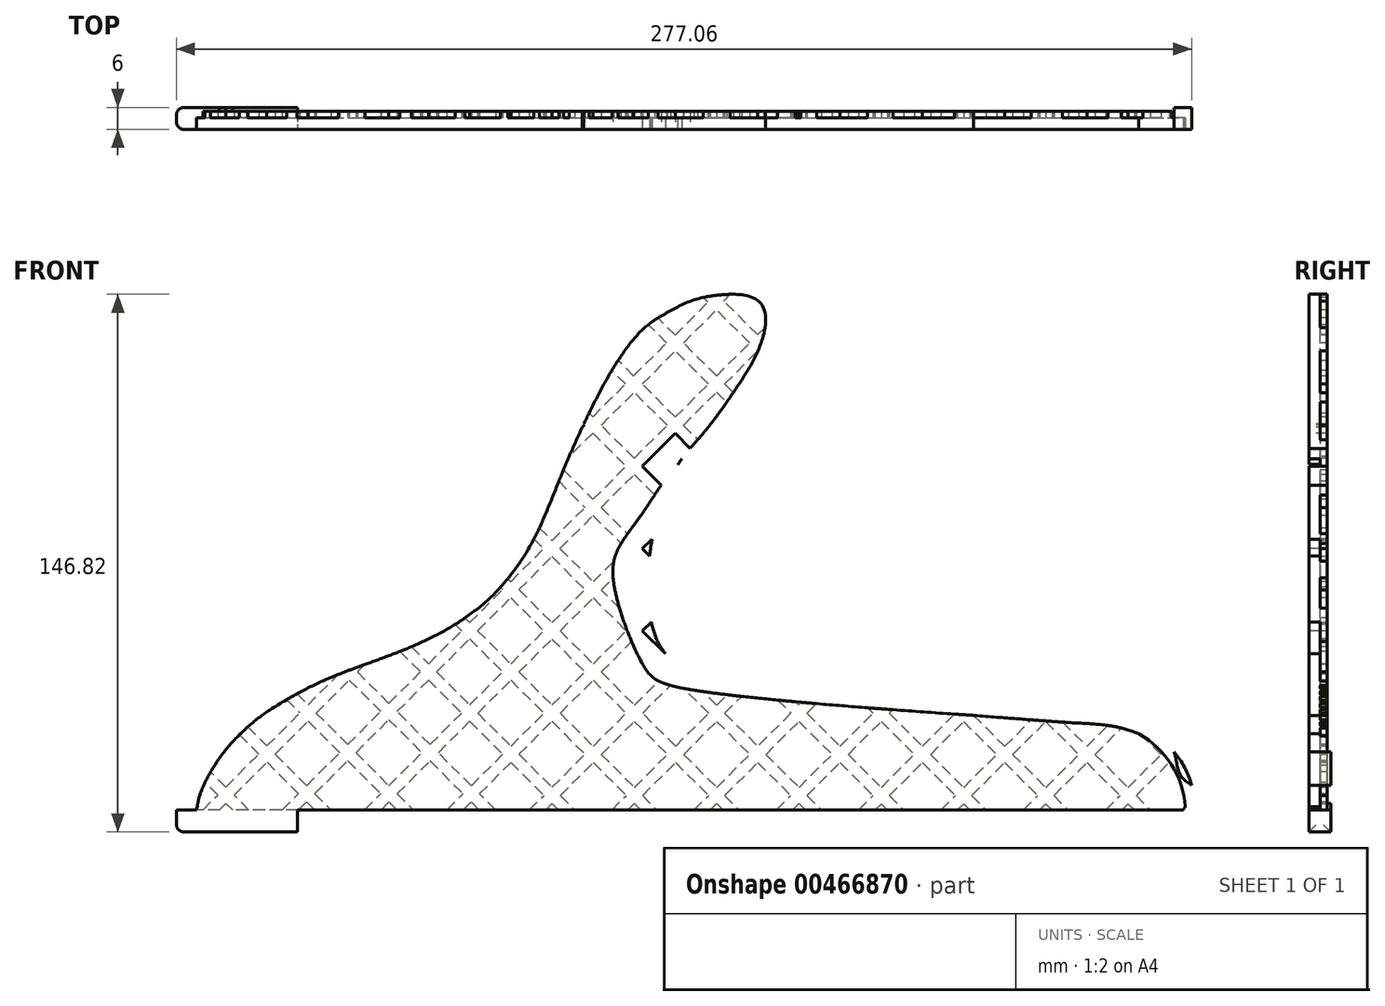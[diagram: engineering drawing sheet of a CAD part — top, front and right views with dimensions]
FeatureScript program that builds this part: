
annotation { "Feature Type Name" : "Feature", "Feature Type Description" : "" }
export const myFeature = defineFeature(function(context is Context, id is Id, definition is map)
    precondition{}
    {
        {
            var Q0;
            Q0=qCreatedBy(makeId("Front.planeOp"),FACE);
            var sketch = newSketch(context, id + "F0", { "sketchPlane" : qUnion([Q0])});
            skLineSegment(sketch, "E0", {"start": v(-116, 0) * mm, "end": v(-116, -6) * mm});
            skLineSegment(sketch, "E1", {"start": v(-116, -6) * mm, "end": v(-83, -6) * mm});
            skLineSegment(sketch, "E2", {"start": v(-83, -6) * mm, "end": v(-83, 0) * mm});
            skLineSegment(sketch, "E3", {"start": v(-83, 0) * mm, "end": v(-82.7, 0) * mm});
            skArc(sketch, "E4", {"start": v(162, 0) * mm, "mid": v(155.8, 16.5) * mm, "end": v(140.24, 24.79) * mm});
            skLineSegment(sketch, "E5", {"start": v(140.24, 24.79) * mm, "end": v(39.58, 33.6) * mm});
            skFitSpline(sketch, "E6", {"points": [v(-116, 0) * mm, v(-106.77, 17.97) * mm, v(-86.19, 34.74) * mm, v(-51.87, 47.68) * mm, v(-30.13, 63.36) * mm, v(-15.89, 87.59) * mm, v(-3.25, 115.08) * mm, v(10.46, 133.67) * mm, v(27.88, 142.86) * mm, v(45.91, 140.16) * mm, v(44.88, 124.4) * mm, v(32.37, 105.05) * mm, v(24.04, 94.4) * mm, v(12.3, 78.31) * mm], "startDerivative": vector(110.14, 372.48) * mm, "endDerivative": vector(-175.67, -307.4) * mm});
            skFitSpline(sketch, "E7", {"points": [v(-110.58, 0) * mm, v(-109.72, 3.92) * mm, v(-104.27, 14.22) * mm, v(-97.47, 21.84) * mm, v(-91.58, 26.62) * mm, v(-79.54, 33.6) * mm, v(-68.24, 38.4) * mm, v(-52.26, 44.4) * mm, v(-40.42, 50.4) * mm, v(-31.67, 56.73) * mm, v(-26.67, 61.88) * mm, v(-19.12, 72.72) * mm, v(-10.73, 92.02) * mm, v(-2.47, 110.27) * mm, v(4.52, 122.74) * mm, v(11.8, 131.72) * mm, v(18.12, 135.9) * mm, v(25.92, 139.48) * mm, v(34.7, 140.8) * mm, v(38.92, 140.55) * mm, v(43.31, 138.54) * mm, v(44.78, 133) * mm, v(42.07, 124.02) * mm, v(36.65, 115) * mm, v(29.24, 104.7) * mm, v(18.05, 91.14) * mm, v(10.55, 80.15) * mm, v(5.27, 72.64) * mm, v(3.17, 63.32) * mm, v(10.92, 40.34) * mm, v(22.95, 33.11) * mm, v(135.88, 23.55) * mm, v(145.48, 22.31) * mm, v(155.41, 17.66) * mm, v(158.63, 8.75) * mm, v(163.79, 4.17) * mm, v(158.83, 0) * mm], "startDerivative": vector(86.06, 309.75) * mm, "endDerivative": vector(-2.43, -186.75) * mm});
            skLineSegment(sketch, "E8", {"start": v(-100.7, 0) * mm, "end": v(-102.52, 1.82) * mm});
            skLineSegment(sketch, "E9", {"start": v(-96.29, 0) * mm, "end": v(-100.32, 4.03) * mm});
            skLineSegment(sketch, "E10", {"start": v(-98.81, 20.56) * mm, "end": v(-93.54, 15.3) * mm});
            skLineSegment(sketch, "E11", {"start": v(-96.53, 22.7) * mm, "end": v(-91.33, 17.5) * mm});
            skLineSegment(sketch, "E12", {"start": v(-85.94, 30.14) * mm, "end": v(-82.32, 26.52) * mm});
            skLineSegment(sketch, "E13", {"start": v(-83.11, 31.73) * mm, "end": v(-80.1, 28.73) * mm});
            skLineSegment(sketch, "E14", {"start": v(-68.85, 35.5) * mm, "end": v(-60.24, 26.89) * mm});
            skLineSegment(sketch, "E15", {"start": v(-28.93, 0) * mm, "end": v(-33.33, 4.4) * mm});
            skLineSegment(sketch, "E16", {"start": v(-55.01, 43.3) * mm, "end": v(-49.42, 37.7) * mm});
            skLineSegment(sketch, "E17", {"start": v(-51.87, 44.57) * mm, "end": v(-47.21, 39.92) * mm});
            skLineSegment(sketch, "E18", {"start": v(-39.95, 50.68) * mm, "end": v(-38.2, 48.93) * mm});
            skLineSegment(sketch, "E19", {"start": v(-37.28, 52.44) * mm, "end": v(-35.99, 51.14) * mm});
            skLineSegment(sketch, "E20", {"start": v(-27.6, 60.79) * mm, "end": v(-26.97, 60.16) * mm});
            skLineSegment(sketch, "E21", {"start": v(-25.58, 63.2) * mm, "end": v(-24.76, 62.37) * mm});
            skLineSegment(sketch, "E22", {"start": v(-18.42, 74.05) * mm, "end": v(-15.75, 71.38) * mm});
            skLineSegment(sketch, "E23", {"start": v(-16.97, 77.02) * mm, "end": v(-13.54, 73.6) * mm});
            skLineSegment(sketch, "E24", {"start": v(-11.66, 89.75) * mm, "end": v(-4.52, 82.6) * mm});
            skLineSegment(sketch, "E25", {"start": v(-10.38, 92.89) * mm, "end": v(-2.31, 84.82) * mm});
            skLineSegment(sketch, "E26", {"start": v(-4.84, 105.38) * mm, "end": v(-4.6, 105.15) * mm});
            skLineSegment(sketch, "E27", {"start": v(-3.4, 108.36) * mm, "end": v(-2.4, 107.36) * mm});
            skLineSegment(sketch, "E28", {"start": v(31.39, 114.1) * mm, "end": v(34.18, 111.35) * mm});
            skLineSegment(sketch, "E29", {"start": v(33.6, 116.3) * mm, "end": v(35.96, 113.98) * mm});
            skLineSegment(sketch, "E30", {"start": v(40.41, 127.54) * mm, "end": v(31.38, 136.54) * mm});
            skLineSegment(sketch, "E31", {"start": v(42.62, 129.75) * mm, "end": v(33.32, 139.01) * mm});
            skLineSegment(sketch, "E32", {"start": v(121.27, 24.16) * mm, "end": v(130.3, 15.15) * mm});
            skLineSegment(sketch, "E33", {"start": v(125.87, 24) * mm, "end": v(132.5, 17.36) * mm});
            skLineSegment(sketch, "E34.trimOffspring", {"start": v(101.57, 25.84) * mm, "end": v(110.05, 17.36) * mm});
            skLineSegment(sketch, "E35.trimOffspring", {"start": v(98.82, 24.16) * mm, "end": v(107.84, 15.15) * mm});
            skLineSegment(sketch, "E36.trimOffspring", {"start": v(78.55, 26.4) * mm, "end": v(87.56, 17.4) * mm});
            skLineSegment(sketch, "E37.trimOffspring", {"start": v(72.62, 27.92) * mm, "end": v(74.13, 26.4) * mm});
            skLineSegment(sketch, "E38.trimOffspring", {"start": v(52.95, 29.56) * mm, "end": v(53.77, 28.74) * mm});
            skLineSegment(sketch, "E39.trimOffspring", {"start": v(48.08, 30) * mm, "end": v(51.68, 26.4) * mm});
            skLineSegment(sketch, "E40", {"start": v(-104.34, 0) * mm, "end": v(-102.52, 1.82) * mm});
            skLineSegment(sketch, "E41", {"start": v(-108.83, 0) * mm, "end": v(-104.77, 4.07) * mm});
            skLineSegment(sketch, "E42", {"start": v(-87.13, 0) * mm, "end": v(-82.7, 4.44) * mm});
            skLineSegment(sketch, "E43.trimOffspring", {"start": v(42.62, 129.75) * mm, "end": v(44.65, 131.77) * mm});
            skLineSegment(sketch, "E44", {"start": v(-82.7, 0) * mm, "end": v(-80.48, 2.23) * mm});
            skLineSegment(sketch, "E45", {"start": v(-5.25, 104.5) * mm, "end": v(-4.6, 105.15) * mm});
            skLineSegment(sketch, "E46", {"start": v(20.08, 129.63) * mm, "end": v(29.08, 138.66) * mm});
            skLineSegment(sketch, "E47.trimOffspring", {"start": v(29.08, 138.66) * mm, "end": v(27.78, 139.96) * mm});
            skLineSegment(sketch, "E48.trimOffspring", {"start": v(33.32, 139.01) * mm, "end": v(35.11, 140.81) * mm});
            skLineSegment(sketch, "E49", {"start": v(-60.19, 0) * mm, "end": v(-58, 2.2) * mm});
            skLineSegment(sketch, "E50", {"start": v(-64.68, 0) * mm, "end": v(-60.24, 4.44) * mm});
            skLineSegment(sketch, "E51", {"start": v(-42.15, 0) * mm, "end": v(-37.75, 4.4) * mm});
            skLineSegment(sketch, "E52", {"start": v(-37.74, 0) * mm, "end": v(-35.54, 2.2) * mm});
            skLineSegment(sketch, "E53", {"start": v(-15.21, 0) * mm, "end": v(-13.46, 1.75) * mm});
            skLineSegment(sketch, "E54", {"start": v(-19.7, 0) * mm, "end": v(-15.7, 4) * mm});
            skLineSegment(sketch, "E55", {"start": v(2.82, 0) * mm, "end": v(6.78, 3.96) * mm});
            skLineSegment(sketch, "E56", {"start": v(7.24, 0) * mm, "end": v(8.99, 1.75) * mm});
            skLineSegment(sketch, "E57", {"start": v(29.69, 0) * mm, "end": v(31.44, 1.75) * mm});
            skLineSegment(sketch, "E58", {"start": v(25.27, 0) * mm, "end": v(29.23, 3.96) * mm});
            skLineSegment(sketch, "E59", {"start": v(47.72, 0) * mm, "end": v(51.68, 3.96) * mm});
            skLineSegment(sketch, "E60", {"start": v(52.14, 0) * mm, "end": v(53.89, 1.75) * mm});
            skLineSegment(sketch, "E61", {"start": v(74.66, 0) * mm, "end": v(76.37, 1.71) * mm});
            skLineSegment(sketch, "E62", {"start": v(70.17, 0) * mm, "end": v(74.13, 3.96) * mm});
            skLineSegment(sketch, "E63", {"start": v(92.7, 0) * mm, "end": v(96.61, 3.92) * mm});
            skLineSegment(sketch, "E64", {"start": v(97.1, 0) * mm, "end": v(98.82, 1.71) * mm});
            skLineSegment(sketch, "E65", {"start": v(119.56, 0) * mm, "end": v(121.27, 1.71) * mm});
            skLineSegment(sketch, "E66", {"start": v(115.14, 0) * mm, "end": v(119.06, 3.92) * mm});
            skLineSegment(sketch, "E67", {"start": v(137.6, 0) * mm, "end": v(141.52, 3.92) * mm});
            skLineSegment(sketch, "E68", {"start": v(142.01, 0) * mm, "end": v(143.73, 1.71) * mm});
            skPoint(sketch, "E69.orphan", {"position": v(103.07, -34.52) * mm});
            skPoint(sketch, "E70.orphan", {"position": v(85.04, -34.52) * mm});
            skPoint(sketch, "E71.orphan", {"position": v(0, -2.82) * mm});
            skLineSegment(sketch, "E72", {"start": v(-83, 0) * mm, "end": v(-100.7, 0) * mm});
            skLineSegment(sketch, "E73.trimOffspring", {"start": v(-104.77, 4.07) * mm, "end": v(-108.22, 7.52) * mm});
            skLineSegment(sketch, "E74.trimOffspring", {"start": v(-102.56, 6.27) * mm, "end": v(-93.54, 15.3) * mm});
            skLineSegment(sketch, "E75.trimOffspring", {"start": v(-102.56, 6.27) * mm, "end": v(-106.68, 10.4) * mm});
            skLineSegment(sketch, "E76.trimOffspring", {"start": v(-100.32, 4.03) * mm, "end": v(-91.3, 13.05) * mm});
            skLineSegment(sketch, "E77.trimOffspring", {"start": v(-91.3, 13.05) * mm, "end": v(-82.7, 4.44) * mm});
            skLineSegment(sketch, "E78.trimOffspring", {"start": v(-89.09, 15.26) * mm, "end": v(-80.48, 6.65) * mm});
            skLineSegment(sketch, "E79.trimOffspring", {"start": v(-91.33, 17.5) * mm, "end": v(-82.32, 26.52) * mm});
            skLineSegment(sketch, "E80.trimOffspring", {"start": v(-89.09, 15.26) * mm, "end": v(-80.07, 24.27) * mm});
            skLineSegment(sketch, "E81.trimOffspring", {"start": v(-80.48, 6.65) * mm, "end": v(-71.47, 15.66) * mm});
            skLineSegment(sketch, "E82.trimOffspring", {"start": v(-78.27, 4.44) * mm, "end": v(-69.26, 13.45) * mm});
            skLineSegment(sketch, "E83.trimOffspring", {"start": v(-78.27, 4.44) * mm, "end": v(-73.83, 0) * mm});
            skLineSegment(sketch, "E84.trimOffspring", {"start": v(-80.48, 2.23) * mm, "end": v(-78.25, 0) * mm});
            skLineSegment(sketch, "E85.trimOffspring", {"start": v(-80.07, 24.27) * mm, "end": v(-71.47, 15.66) * mm});
            skLineSegment(sketch, "E86.trimOffspring", {"start": v(-77.86, 26.48) * mm, "end": v(-69.26, 17.87) * mm});
            skLineSegment(sketch, "E87.trimOffspring", {"start": v(-80.1, 28.73) * mm, "end": v(-71.8, 37.04) * mm});
            skLineSegment(sketch, "E88.trimOffspring", {"start": v(-77.86, 26.48) * mm, "end": v(-68.85, 35.5) * mm});
            skLineSegment(sketch, "E89.trimOffspring", {"start": v(-69.26, 17.87) * mm, "end": v(-60.24, 26.89) * mm});
            skLineSegment(sketch, "E90.trimOffspring", {"start": v(-67.05, 15.66) * mm, "end": v(-58.03, 24.68) * mm});
            skLineSegment(sketch, "E91.trimOffspring", {"start": v(-67.05, 15.66) * mm, "end": v(-58.03, 6.65) * mm});
            skLineSegment(sketch, "E92.trimOffspring", {"start": v(-69.26, 13.45) * mm, "end": v(-60.24, 4.44) * mm});
            skLineSegment(sketch, "E93.trimOffspring", {"start": v(-58, 2.2) * mm, "end": v(-55.8, 0) * mm});
            skLineSegment(sketch, "E94.trimOffspring", {"start": v(-58.03, 6.65) * mm, "end": v(-49.01, 15.66) * mm});
            skLineSegment(sketch, "E95.trimOffspring", {"start": v(-55.78, 4.4) * mm, "end": v(-51.38, 0) * mm});
            skLineSegment(sketch, "E96.trimOffspring", {"start": v(-55.78, 4.4) * mm, "end": v(-46.77, 13.42) * mm});
            skLineSegment(sketch, "E97.trimOffspring", {"start": v(-66.64, 37.7) * mm, "end": v(-64.61, 39.73) * mm});
            skLineSegment(sketch, "E98.trimOffspring", {"start": v(-58.03, 29.1) * mm, "end": v(-49.42, 37.7) * mm});
            skLineSegment(sketch, "E99.trimOffspring", {"start": v(-55.82, 26.89) * mm, "end": v(-47.21, 35.5) * mm});
            skLineSegment(sketch, "E100.trimOffspring", {"start": v(-58.03, 29.1) * mm, "end": v(-66.64, 37.7) * mm});
            skLineSegment(sketch, "E101.trimOffspring", {"start": v(-58.03, 24.68) * mm, "end": v(-49.01, 15.66) * mm});
            skLineSegment(sketch, "E102.trimOffspring", {"start": v(-46.8, 17.87) * mm, "end": v(-38.2, 26.48) * mm});
            skLineSegment(sketch, "E103.trimOffspring", {"start": v(-44.56, 15.63) * mm, "end": v(-35.95, 24.24) * mm});
            skLineSegment(sketch, "E104.trimOffspring", {"start": v(-46.8, 17.87) * mm, "end": v(-55.82, 26.89) * mm});
            skLineSegment(sketch, "E105.trimOffspring", {"start": v(-46.77, 13.42) * mm, "end": v(-37.75, 4.4) * mm});
            skLineSegment(sketch, "E106.trimOffspring", {"start": v(-47.21, 39.92) * mm, "end": v(-38.2, 48.93) * mm});
            skLineSegment(sketch, "E107.trimOffspring", {"start": v(-45, 37.7) * mm, "end": v(-35.99, 28.7) * mm});
            skLineSegment(sketch, "E108.trimOffspring", {"start": v(-47.21, 35.5) * mm, "end": v(-38.2, 26.48) * mm});
            skLineSegment(sketch, "E109.trimOffspring", {"start": v(-45, 37.7) * mm, "end": v(-35.99, 46.72) * mm});
            skLineSegment(sketch, "E110.trimOffspring", {"start": v(-35.99, 28.7) * mm, "end": v(-26.97, 37.7) * mm});
            skLineSegment(sketch, "E111.trimOffspring", {"start": v(-33.74, 26.45) * mm, "end": v(-24.73, 35.46) * mm});
            skLineSegment(sketch, "E112.trimOffspring", {"start": v(-33.74, 26.45) * mm, "end": v(-24.73, 17.43) * mm});
            skLineSegment(sketch, "E113.trimOffspring", {"start": v(-35.95, 24.24) * mm, "end": v(-26.94, 15.22) * mm});
            skLineSegment(sketch, "E114.trimOffspring", {"start": v(-35.99, 46.72) * mm, "end": v(-26.97, 37.7) * mm});
            skLineSegment(sketch, "E115.trimOffspring", {"start": v(-35.99, 51.14) * mm, "end": v(-26.97, 60.16) * mm});
            skLineSegment(sketch, "E116.trimOffspring", {"start": v(-33.78, 48.93) * mm, "end": v(-24.76, 39.92) * mm});
            skLineSegment(sketch, "E117.trimOffspring", {"start": v(-33.78, 48.93) * mm, "end": v(-24.76, 57.95) * mm});
            skLineSegment(sketch, "E118.trimOffspring", {"start": v(-24.76, 39.92) * mm, "end": v(-15.75, 48.93) * mm});
            skLineSegment(sketch, "E119.trimOffspring", {"start": v(-22.52, 37.67) * mm, "end": v(-13.5, 46.69) * mm});
            skLineSegment(sketch, "E120.trimOffspring", {"start": v(-22.52, 37.67) * mm, "end": v(-13.5, 28.65) * mm});
            skLineSegment(sketch, "E121.trimOffspring", {"start": v(-24.73, 35.46) * mm, "end": v(-15.7, 26.45) * mm});
            skLineSegment(sketch, "E122.trimOffspring", {"start": v(-24.73, 17.43) * mm, "end": v(-15.7, 26.45) * mm});
            skLineSegment(sketch, "E123.trimOffspring", {"start": v(-22.52, 15.22) * mm, "end": v(-13.5, 24.24) * mm});
            skLineSegment(sketch, "E124.trimOffspring", {"start": v(-22.52, 15.22) * mm, "end": v(-13.5, 6.2) * mm});
            skLineSegment(sketch, "E125.trimOffspring", {"start": v(-24.73, 13.01) * mm, "end": v(-15.7, 4) * mm});
            skLineSegment(sketch, "E126.trimOffspring", {"start": v(-35.54, 6.61) * mm, "end": v(-44.56, 15.63) * mm});
            skLineSegment(sketch, "E127.trimOffspring", {"start": v(-35.54, 6.61) * mm, "end": v(-26.94, 15.22) * mm});
            skLineSegment(sketch, "E128.trimOffspring", {"start": v(-35.54, 2.2) * mm, "end": v(-33.35, 0) * mm});
            skLineSegment(sketch, "E129.trimOffspring", {"start": v(-33.33, 4.4) * mm, "end": v(-24.73, 13.01) * mm});
            skLineSegment(sketch, "E130.trimOffspring", {"start": v(-13.5, 6.2) * mm, "end": v(-4.48, 15.22) * mm});
            skLineSegment(sketch, "E131.trimOffspring", {"start": v(-11.25, 3.96) * mm, "end": v(-2.24, 12.97) * mm});
            skLineSegment(sketch, "E132.trimOffspring", {"start": v(-13.46, 1.75) * mm, "end": v(-11.72, 0) * mm});
            skLineSegment(sketch, "E133.trimOffspring", {"start": v(-11.25, 3.96) * mm, "end": v(-7.3, 0) * mm});
            skLineSegment(sketch, "E134.trimOffspring", {"start": v(-2.27, 17.43) * mm, "end": v(6.74, 26.45) * mm});
            skLineSegment(sketch, "E135.trimOffspring", {"start": v(-0.03, 15.18) * mm, "end": v(8.99, 24.2) * mm});
            skLineSegment(sketch, "E136.trimOffspring", {"start": v(-2.24, 12.97) * mm, "end": v(6.78, 3.96) * mm});
            skLineSegment(sketch, "E137.trimOffspring", {"start": v(-0.03, 15.18) * mm, "end": v(8.99, 6.17) * mm});
            skLineSegment(sketch, "E138.trimOffspring", {"start": v(-11.3, 26.45) * mm, "end": v(-2.27, 17.43) * mm});
            skLineSegment(sketch, "E139.trimOffspring", {"start": v(-13.5, 24.24) * mm, "end": v(-4.48, 15.22) * mm});
            skLineSegment(sketch, "E140.trimOffspring", {"start": v(-13.5, 28.65) * mm, "end": v(-4.48, 37.67) * mm});
            skLineSegment(sketch, "E141.trimOffspring", {"start": v(-11.3, 26.45) * mm, "end": v(-2.27, 35.46) * mm});
            skLineSegment(sketch, "E142.trimOffspring", {"start": v(-24.76, 57.95) * mm, "end": v(-15.75, 48.93) * mm});
            skLineSegment(sketch, "E143.trimOffspring", {"start": v(-24.76, 62.37) * mm, "end": v(-15.75, 71.38) * mm});
            skLineSegment(sketch, "E144.trimOffspring", {"start": v(-22.55, 60.16) * mm, "end": v(-13.54, 51.14) * mm});
            skLineSegment(sketch, "E145.trimOffspring", {"start": v(-22.55, 60.16) * mm, "end": v(-13.54, 69.17) * mm});
            skLineSegment(sketch, "E146.trimOffspring", {"start": v(-13.54, 69.17) * mm, "end": v(-4.52, 60.16) * mm});
            skLineSegment(sketch, "E147.trimOffspring", {"start": v(-13.54, 73.6) * mm, "end": v(-4.52, 82.6) * mm});
            skLineSegment(sketch, "E148.trimOffspring", {"start": v(-11.33, 71.38) * mm, "end": v(-2.27, 62.33) * mm});
            skLineSegment(sketch, "E149.trimOffspring", {"start": v(-11.33, 71.38) * mm, "end": v(-2.31, 80.4) * mm});
            skLineSegment(sketch, "E150.trimOffspring", {"start": v(-0.06, 60.12) * mm, "end": v(8.95, 69.14) * mm});
            skLineSegment(sketch, "E151.trimOffspring", {"start": v(-2.27, 57.91) * mm, "end": v(6.74, 48.9) * mm});
            skLineSegment(sketch, "E152.trimOffspring", {"start": v(-11.3, 48.9) * mm, "end": v(-2.27, 39.88) * mm});
            skLineSegment(sketch, "E153.trimOffspring", {"start": v(-13.54, 51.14) * mm, "end": v(-4.52, 60.16) * mm});
            skLineSegment(sketch, "E154.trimOffspring", {"start": v(-13.5, 46.69) * mm, "end": v(-4.48, 37.67) * mm});
            skLineSegment(sketch, "E155.trimOffspring", {"start": v(-11.3, 48.9) * mm, "end": v(-2.27, 57.91) * mm});
            skLineSegment(sketch, "E156.trimOffspring", {"start": v(-2.27, 39.88) * mm, "end": v(6.74, 48.9) * mm});
            skLineSegment(sketch, "E157.trimOffspring", {"start": v(-0.06, 37.67) * mm, "end": v(8.99, 28.62) * mm});
            skLineSegment(sketch, "E158.trimOffspring", {"start": v(-2.27, 35.46) * mm, "end": v(6.74, 26.45) * mm});
            skLineSegment(sketch, "E159.trimOffspring", {"start": v(22.5, 15.27) * mm, "end": v(31.44, 24.2) * mm});
            skLineSegment(sketch, "E160.trimOffspring", {"start": v(8.99, 24.2) * mm, "end": v(18, 15.18) * mm});
            skLineSegment(sketch, "E161.trimOffspring", {"start": v(20.21, 12.97) * mm, "end": v(29.23, 3.96) * mm});
            skLineSegment(sketch, "E162.trimOffspring", {"start": v(22.42, 15.18) * mm, "end": v(31.44, 6.17) * mm});
            skLineSegment(sketch, "E163.trimOffspring", {"start": v(20.21, 17.4) * mm, "end": v(29.23, 26.4) * mm});
            skLineSegment(sketch, "E164.trimOffspring", {"start": v(22.42, 15.18) * mm, "end": v(31.44, 24.2) * mm});
            skLineSegment(sketch, "E165.trimOffspring", {"start": v(31.44, 24.2) * mm, "end": v(40.45, 15.18) * mm});
            skLineSegment(sketch, "E166.trimOffspring", {"start": v(33.65, 26.4) * mm, "end": v(42.66, 17.4) * mm});
            skLineSegment(sketch, "E167.trimOffspring", {"start": v(33.65, 26.4) * mm, "end": v(38.25, 31.02) * mm});
            skLineSegment(sketch, "E168.trimOffspring", {"start": v(44.87, 15.18) * mm, "end": v(53.89, 6.17) * mm});
            skLineSegment(sketch, "E169.trimOffspring", {"start": v(42.66, 12.97) * mm, "end": v(51.68, 3.96) * mm});
            skLineSegment(sketch, "E170.trimOffspring", {"start": v(44.87, 15.18) * mm, "end": v(53.89, 24.2) * mm});
            skLineSegment(sketch, "E171.trimOffspring", {"start": v(53.89, 24.2) * mm, "end": v(62.9, 15.18) * mm});
            skLineSegment(sketch, "E172.trimOffspring", {"start": v(56.1, 26.4) * mm, "end": v(65.11, 17.4) * mm});
            skLineSegment(sketch, "E173.trimOffspring", {"start": v(53.77, 28.74) * mm, "end": v(54.45, 29.42) * mm});
            skLineSegment(sketch, "E174.trimOffspring", {"start": v(56.1, 26.4) * mm, "end": v(58.73, 29.05) * mm});
            skLineSegment(sketch, "E175.trimOffspring", {"start": v(56.1, 3.96) * mm, "end": v(60.06, 0) * mm});
            skLineSegment(sketch, "E176.trimOffspring", {"start": v(53.89, 6.17) * mm, "end": v(62.9, 15.18) * mm});
            skLineSegment(sketch, "E177.trimOffspring", {"start": v(53.89, 1.75) * mm, "end": v(55.64, 0) * mm});
            skLineSegment(sketch, "E178.trimOffspring", {"start": v(56.1, 3.96) * mm, "end": v(65.11, 12.97) * mm});
            skLineSegment(sketch, "E179.trimOffspring", {"start": v(65.11, 17.4) * mm, "end": v(74.13, 26.4) * mm});
            skLineSegment(sketch, "E180.trimOffspring", {"start": v(67.32, 15.18) * mm, "end": v(76.34, 6.17) * mm});
            skLineSegment(sketch, "E181.trimOffspring", {"start": v(67.32, 15.18) * mm, "end": v(76.34, 24.2) * mm});
            skLineSegment(sketch, "E182.trimOffspring", {"start": v(65.11, 12.97) * mm, "end": v(74.13, 3.96) * mm});
            skLineSegment(sketch, "E183.trimOffspring", {"start": v(76.34, 6.17) * mm, "end": v(85.35, 15.18) * mm});
            skLineSegment(sketch, "E184.trimOffspring", {"start": v(78.58, 3.92) * mm, "end": v(82.5, 0) * mm});
            skLineSegment(sketch, "E185.trimOffspring", {"start": v(76.37, 1.71) * mm, "end": v(78.09, 0) * mm});
            skLineSegment(sketch, "E186.trimOffspring", {"start": v(78.58, 3.92) * mm, "end": v(87.6, 12.94) * mm});
            skLineSegment(sketch, "E187.trimOffspring", {"start": v(87.6, 12.94) * mm, "end": v(96.61, 3.92) * mm});
            skLineSegment(sketch, "E188.trimOffspring", {"start": v(78.55, 26.4) * mm, "end": v(79.53, 27.4) * mm});
            skLineSegment(sketch, "E189.trimOffspring", {"start": v(76.34, 24.2) * mm, "end": v(85.35, 15.18) * mm});
            skLineSegment(sketch, "E190.trimOffspring", {"start": v(89.8, 15.15) * mm, "end": v(98.82, 24.16) * mm});
            skLineSegment(sketch, "E191.trimOffspring", {"start": v(89.8, 15.15) * mm, "end": v(98.82, 6.13) * mm});
            skLineSegment(sketch, "E192.trimOffspring", {"start": v(87.56, 17.4) * mm, "end": v(96.36, 26.2) * mm});
            skLineSegment(sketch, "E193.trimOffspring", {"start": v(110.05, 17.36) * mm, "end": v(117.32, 24.63) * mm});
            skLineSegment(sketch, "E194.trimOffspring", {"start": v(112.26, 15.15) * mm, "end": v(121.27, 6.13) * mm});
            skLineSegment(sketch, "E195.trimOffspring", {"start": v(112.26, 15.15) * mm, "end": v(121.27, 24.16) * mm});
            skLineSegment(sketch, "E196.trimOffspring", {"start": v(110.05, 12.94) * mm, "end": v(119.06, 3.92) * mm});
            skLineSegment(sketch, "E197.trimOffspring", {"start": v(101.03, 3.92) * mm, "end": v(104.96, 0) * mm});
            skLineSegment(sketch, "E198.trimOffspring", {"start": v(98.82, 6.13) * mm, "end": v(107.84, 15.15) * mm});
            skLineSegment(sketch, "E199.trimOffspring", {"start": v(98.82, 1.71) * mm, "end": v(100.54, 0) * mm});
            skLineSegment(sketch, "E200.trimOffspring", {"start": v(101.03, 3.92) * mm, "end": v(110.05, 12.94) * mm});
            skLineSegment(sketch, "E201.trimOffspring", {"start": v(132.5, 17.36) * mm, "end": v(138.23, 23.1) * mm});
            skLineSegment(sketch, "E202.trimOffspring", {"start": v(134.7, 15.15) * mm, "end": v(141.93, 22.37) * mm});
            skLineSegment(sketch, "E203.trimOffspring", {"start": v(134.7, 15.15) * mm, "end": v(143.73, 6.13) * mm});
            skLineSegment(sketch, "E204.trimOffspring", {"start": v(132.5, 12.94) * mm, "end": v(141.52, 3.92) * mm});
            skLineSegment(sketch, "E205.trimOffspring", {"start": v(123.48, 3.92) * mm, "end": v(127.4, 0) * mm});
            skLineSegment(sketch, "E206.trimOffspring", {"start": v(121.27, 1.71) * mm, "end": v(122.99, 0) * mm});
            skLineSegment(sketch, "E207.trimOffspring", {"start": v(121.27, 6.13) * mm, "end": v(130.3, 15.15) * mm});
            skLineSegment(sketch, "E208.trimOffspring", {"start": v(123.48, 3.92) * mm, "end": v(132.5, 12.94) * mm});
            skLineSegment(sketch, "E209.trimOffspring", {"start": v(143.73, 6.13) * mm, "end": v(152.74, 15.15) * mm});
            skLineSegment(sketch, "E210.trimOffspring", {"start": v(145.93, 3.92) * mm, "end": v(154.95, 12.94) * mm});
            skLineSegment(sketch, "E211.trimOffspring", {"start": v(145.93, 3.92) * mm, "end": v(149.86, 0) * mm});
            skLineSegment(sketch, "E212.trimOffspring", {"start": v(143.73, 1.71) * mm, "end": v(145.44, 0) * mm});
            skLineSegment(sketch, "E213.trimOffspring", {"start": v(-2.31, 84.82) * mm, "end": v(6.7, 93.83) * mm});
            skLineSegment(sketch, "E214.trimOffspring", {"start": v(-0.1, 82.6) * mm, "end": v(8.92, 91.62) * mm});
            skLineSegment(sketch, "E215.trimOffspring", {"start": v(-2.4, 107.36) * mm, "end": v(6.54, 116.3) * mm});
            skLineSegment(sketch, "E216.trimOffspring", {"start": v(-2.4, 102.94) * mm, "end": v(6.7, 93.83) * mm});
            skLineSegment(sketch, "E217.trimOffspring", {"start": v(-0.1, 105.06) * mm, "end": v(8.91, 114.08) * mm});
            skLineSegment(sketch, "E218.trimOffspring", {"start": v(6.54, 116.3) * mm, "end": v(2.82, 120.02) * mm});
            skLineSegment(sketch, "E219.trimOffspring", {"start": v(8.75, 118.5) * mm, "end": v(17.77, 127.52) * mm});
            skLineSegment(sketch, "E220.trimOffspring", {"start": v(8.75, 118.5) * mm, "end": v(4.52, 122.74) * mm});
            skLineSegment(sketch, "E221.trimOffspring", {"start": v(11.12, 116.29) * mm, "end": v(20.15, 125.31) * mm});
            skLineSegment(sketch, "E222.trimOffspring", {"start": v(17.93, 105.06) * mm, "end": v(8.91, 114.08) * mm});
            skLineSegment(sketch, "E223.trimOffspring", {"start": v(22.37, 105.08) * mm, "end": v(31.39, 114.1) * mm});
            skLineSegment(sketch, "E224.trimOffspring", {"start": v(20.14, 107.27) * mm, "end": v(11.12, 116.29) * mm});
            skLineSegment(sketch, "E225.trimOffspring", {"start": v(29.19, 116.32) * mm, "end": v(20.15, 125.31) * mm});
            skLineSegment(sketch, "E226.trimOffspring", {"start": v(31.4, 118.52) * mm, "end": v(22.38, 127.5) * mm});
            skLineSegment(sketch, "E227.trimOffspring", {"start": v(33.6, 116.3) * mm, "end": v(42.7, 125.42) * mm});
            skLineSegment(sketch, "E228.trimOffspring", {"start": v(31.4, 118.52) * mm, "end": v(40.41, 127.54) * mm});
            skLineSegment(sketch, "E229.trimOffspring", {"start": v(22.38, 127.5) * mm, "end": v(31.38, 136.54) * mm});
            skLineSegment(sketch, "E230.trimOffspring", {"start": v(17.77, 127.52) * mm, "end": v(12.76, 132.53) * mm});
            skLineSegment(sketch, "E231.trimOffspring", {"start": v(20.08, 129.63) * mm, "end": v(15.37, 134.34) * mm});
            skLineSegment(sketch, "E232.trimOffspring", {"start": v(20.14, 107.27) * mm, "end": v(29.19, 116.32) * mm});
            skLineSegment(sketch, "E233.trimOffspring", {"start": v(-104.34, 0) * mm, "end": v(-116, 0) * mm});
            skLineSegment(sketch, "E234.trimOffspring", {"start": v(-78.25, 0) * mm, "end": v(159.43, 0) * mm});
            skLineSegment(sketch, "E235", {"start": v(-82.7, 0) * mm, "end": v(-78.25, 0) * mm});
            skLineSegment(sketch, "E236.trimOffspring", {"start": v(31.44, 6.17) * mm, "end": v(40.45, 15.18) * mm});
            skLineSegment(sketch, "E237.trimOffspring", {"start": v(33.65, 3.96) * mm, "end": v(42.66, 12.97) * mm});
            skLineSegment(sketch, "E238.trimOffspring", {"start": v(31.44, 1.75) * mm, "end": v(33.19, 0) * mm});
            skLineSegment(sketch, "E239.trimOffspring", {"start": v(33.65, 3.96) * mm, "end": v(37.6, 0) * mm});
            skLineSegment(sketch, "E240.trimOffspring", {"start": v(11.2, 3.96) * mm, "end": v(15.15, 0) * mm});
            skLineSegment(sketch, "E241.trimOffspring", {"start": v(8.99, 6.17) * mm, "end": v(18, 15.18) * mm});
            skLineSegment(sketch, "E242.trimOffspring", {"start": v(8.99, 1.75) * mm, "end": v(10.74, 0) * mm});
            skLineSegment(sketch, "E243.trimOffspring", {"start": v(11.2, 3.96) * mm, "end": v(20.21, 12.97) * mm});
            skFitSpline(sketch, "E244", {"points": [v(39.58, 33.6) * mm, v(29.2, 36.2) * mm, v(24.64, 38.85) * mm, v(19.31, 45.16) * mm, v(16.43, 50.98) * mm, v(15.23, 59.34) * mm, v(15.57, 67.86) * mm, v(16.67, 75.73) * mm, v(18.02, 81.55) * mm, v(20.18, 87.66) * mm, v(24.04, 94.4) * mm], "startDerivative": vector(-99.51, 16.75) * mm, "endDerivative": vector(46.52, 71.35) * mm});
            skFitSpline(sketch, "E245", {"points": [v(38.25, 31.02) * mm, v(27.62, 33.52) * mm, v(22.42, 37.1) * mm, v(17.07, 43.11) * mm, v(14.09, 49.32) * mm, v(12.87, 58.46) * mm, v(12.92, 67) * mm, v(13.91, 74.62) * mm, v(15.42, 81.11) * mm, v(17.59, 88.06) * mm, v(21.9, 95.95) * mm], "startDerivative": vector(-99.47, 17.06) * mm, "endDerivative": vector(46.53, 71.34) * mm});
            skFitSpline(sketch, "E246", {"points": [v(-110.58, 0) * mm, v(-109.72, 3.92) * mm, v(-104.27, 14.22) * mm, v(-97.47, 21.84) * mm, v(-91.58, 26.62) * mm, v(-79.54, 33.6) * mm, v(-68.24, 38.4) * mm, v(-52.26, 44.4) * mm, v(-40.42, 50.4) * mm, v(-31.67, 56.73) * mm, v(-26.67, 61.88) * mm, v(-19.12, 72.72) * mm, v(-10.73, 92.02) * mm, v(-2.47, 110.27) * mm, v(4.52, 122.74) * mm, v(11.8, 131.72) * mm, v(18.12, 135.9) * mm, v(25.92, 139.48) * mm, v(34.7, 140.8) * mm, v(38.92, 140.55) * mm, v(43.31, 138.54) * mm, v(44.78, 133) * mm, v(42.07, 124.02) * mm, v(36.65, 115) * mm, v(29.24, 104.7) * mm, v(18.05, 91.14) * mm, v(10.55, 80.15) * mm, v(5.27, 72.64) * mm, v(3.17, 63.32) * mm, v(10.92, 40.34) * mm, v(22.95, 33.11) * mm, v(135.88, 23.55) * mm, v(145.48, 22.31) * mm, v(155.41, 17.66) * mm, v(158.63, 8.75) * mm, v(163.79, 4.17) * mm, v(158.83, 0) * mm], "startDerivative": vector(86.06, 309.75) * mm, "endDerivative": vector(-2.43, -186.75) * mm});
            skLineSegment(sketch, "E247", {"start": v(8.99, 28.62) * mm, "end": v(18, 37.64) * mm});
            skLineSegment(sketch, "E248", {"start": v(20.21, 17.4) * mm, "end": v(11.2, 26.4) * mm});
            skLineSegment(sketch, "E249", {"start": v(11.2, 26.4) * mm, "end": v(20.21, 35.43) * mm});
            skLineSegment(sketch, "E250", {"start": v(29.23, 26.4) * mm, "end": v(20.21, 35.43) * mm});
            skLineSegment(sketch, "E251", {"start": v(31.44, 28.62) * mm, "end": v(25.33, 34.73) * mm});
            skLineSegment(sketch, "E252", {"start": v(31.44, 28.62) * mm, "end": v(34.5, 31.68) * mm});
            skLineSegment(sketch, "E253", {"start": v(18, 37.64) * mm, "end": v(8.95, 46.69) * mm});
            skLineSegment(sketch, "E254", {"start": v(-0.06, 37.67) * mm, "end": v(8.95, 46.69) * mm});
            skLineSegment(sketch, "E255", {"start": v(17.41, 42.64) * mm, "end": v(11.16, 48.9) * mm});
            skLineSegment(sketch, "E256", {"start": v(8.95, 51.1) * mm, "end": v(13.1, 55.25) * mm});
            skLineSegment(sketch, "E257", {"start": v(11.16, 48.9) * mm, "end": v(13.62, 51.36) * mm});
            skLineSegment(sketch, "E258.trimOffspring", {"start": v(8.95, 51.1) * mm, "end": v(-0.06, 60.12) * mm});
            skPoint(sketch, "E259.orphan", {"position": v(6.74, 48.9) * mm});
            skLineSegment(sketch, "E260", {"start": v(-2.27, 62.33) * mm, "end": v(6.74, 71.35) * mm});
            skLineSegment(sketch, "E261", {"start": v(-2.31, 80.4) * mm, "end": v(6.74, 71.35) * mm});
            skLineSegment(sketch, "E262", {"start": v(-0.1, 82.6) * mm, "end": v(8.95, 73.56) * mm});
            skLineSegment(sketch, "E263.trimOffspring", {"start": v(8.95, 73.56) * mm, "end": v(15.05, 79.65) * mm});
            skLineSegment(sketch, "E264", {"start": v(8.95, 69.14) * mm, "end": v(12.83, 65.26) * mm});
            skLineSegment(sketch, "E265", {"start": v(11.16, 71.35) * mm, "end": v(13.13, 69.37) * mm});
            skLineSegment(sketch, "E266.trimOffspring", {"start": v(11.16, 71.35) * mm, "end": v(13.8, 73.98) * mm});
            skLineSegment(sketch, "E267", {"start": v(22.37, 105.08) * mm, "end": v(22.35, 105.06) * mm});
            skLineSegment(sketch, "E268", {"start": v(21.9, 95.95) * mm, "end": v(20.9, 94.39) * mm});
            skLineSegment(sketch, "E269", {"start": v(8.91, 96.04) * mm, "end": v(17.93, 105.06) * mm});
            skLineSegment(sketch, "E270", {"start": v(20.14, 102.85) * mm, "end": v(24.25, 98.74) * mm});
            skLineSegment(sketch, "E271", {"start": v(22.35, 105.06) * mm, "end": v(26.28, 101.12) * mm});
            skLineSegment(sketch, "E272.trimOffspring", {"start": v(20.14, 102.85) * mm, "end": v(11.12, 93.83) * mm});
            skLineSegment(sketch, "E273", {"start": v(8.91, 96.04) * mm, "end": v(-0.1, 105.06) * mm});
            skLineSegment(sketch, "E274", {"start": v(8.92, 91.62) * mm, "end": v(16.27, 84.27) * mm});
            skLineSegment(sketch, "E275", {"start": v(11.12, 93.83) * mm, "end": v(17.39, 87.57) * mm});
            skLineSegment(sketch, "E276", {"start": v(-2.4, 102.94) * mm, "end": v(-8.86, 96.47) * mm});
            skArc(sketch, "E277", {"start": v(159.43, 0) * mm, "mid": v(155.74, 12.08) * mm, "end": v(146.63, 20.82) * mm});
            skLineSegment(sketch, "E278", {"start": v(162, 0) * mm, "end": v(159.43, 0) * mm});
            skFitSpline(sketch, "E279", {"points": [v(146.63, 20.82) * mm, v(138.78, 23.01) * mm, v(129, 23.8) * mm, v(118.27, 24.55) * mm, v(101.57, 25.84) * mm], "startDerivative": vector(-35.56, 14.44) * mm, "endDerivative": vector(-70.12, 5.6) * mm});
            skLineSegment(sketch, "E280", {"start": v(152.74, 15.15) * mm, "end": v(147.72, 20.17) * mm});
            skLineSegment(sketch, "E281", {"start": v(154.95, 12.94) * mm, "end": v(155.63, 12.26) * mm});
            skLineSegment(sketch, "E282", {"start": v(51.68, 26.4) * mm, "end": v(42.66, 17.4) * mm});
            skSolve(sketch);
        }
        {
            var Q0;
            {var subQ46=sQuery(id+"F0.wireOp",EDGE,"E4");Q0=makeQuery(id+"F0.imprint","IMPRINT",FACE,{"disambiguationData":[TD([[makeQuery(id+"F0.imprint","IMPRINT",EDGE,{"derivedFrom":subQ46}),1.0]])]});}
            var Q1;
            {var subQ9=sQuery(id+"F0.wireOp",EDGE,"E0");Q1=makeQuery(id+"F0.imprint","IMPRINT",FACE,{"disambiguationData":[TD([[makeQuery(id+"F0.imprint","IMPRINT",EDGE,{"derivedFrom":subQ9}),1.0]])]});}
            extrude(context, id + "F1", {"entities" : qUnion([Q0, Q1]), "oppositeDirection" : true, "depth" : 6 * mm});
        }
        {
            var Q0;
            {var subQ44=sQuery(id+"F0.wireOp",EDGE,"E3");Q0=makeQuery(id+"F0.imprint","IMPRINT",FACE,{"disambiguationData":[TD([[makeQuery(id+"F0.imprint","IMPRINT",EDGE,{"derivedFrom":subQ44}),1.0]])]});}
            extrude(context, id + "F2", {"entities" : qUnion([Q0]), "operationType" : NewBodyOperationType.ADD, "oppositeDirection" : true, "depth" : 5 * mm});
        }
        {
            var Q0;
            {var subQ0=sQuery(id+"F0.wireOp",EDGE,"E10");Q0=makeQuery(id+"F0.imprint","IMPRINT",FACE,{"disambiguationData":[TD([[makeQuery(id+"F0.imprint","IMPRINT",EDGE,{"derivedFrom":subQ0}),-1.0]])]});}
            var Q1;
            {var subQ4=sQuery(id+"F0.wireOp",EDGE,"E41");Q1=makeQuery(id+"F0.imprint","IMPRINT",FACE,{"disambiguationData":[TD([[makeQuery(id+"F0.imprint","IMPRINT",EDGE,{"derivedFrom":subQ4}),1.0]])]});}
            var Q2;
            {var subQ1=sQuery(id+"F0.wireOp",EDGE,"E9");Q2=makeQuery(id+"F0.imprint","IMPRINT",FACE,{"disambiguationData":[TD([[makeQuery(id+"F0.imprint","IMPRINT",EDGE,{"derivedFrom":subQ1}),-1.0]])]});}
            var Q3;
            Q3=makeQuery(id+"F0.imprint","IMPRINT",FACE,{"disambiguationData":[TD([[makeQuery(id+"F0.imprint","IMPRINT",EDGE,{"derivedFrom":sQuery(id+"F0.wireOp",EDGE,"E78.trimOffspring")}),1.0]])]});
            var Q4;
            {var subQ0=sQuery(id+"F0.wireOp",EDGE,"E11");Q4=makeQuery(id+"F0.imprint","IMPRINT",FACE,{"disambiguationData":[TD([[makeQuery(id+"F0.imprint","IMPRINT",EDGE,{"derivedFrom":subQ0}),1.0]])]});}
            var Q5;
            {var subQ0=sQuery(id+"F0.wireOp",EDGE,"E13");Q5=makeQuery(id+"F0.imprint","IMPRINT",FACE,{"disambiguationData":[TD([[makeQuery(id+"F0.imprint","IMPRINT",EDGE,{"derivedFrom":subQ0}),1.0]])]});}
            var Q6;
            Q6=makeQuery(id+"F0.imprint","IMPRINT",FACE,{"disambiguationData":[TD([[makeQuery(id+"F0.imprint","IMPRINT",EDGE,{"derivedFrom":sQuery(id+"F0.wireOp",EDGE,"E14")}),-1.0]])]});
            var Q7;
            {var subQ1=sQuery(id+"F0.wireOp",EDGE,"E16");Q7=makeQuery(id+"F0.imprint","IMPRINT",FACE,{"disambiguationData":[TD([[makeQuery(id+"F0.imprint","IMPRINT",EDGE,{"derivedFrom":subQ1}),-1.0]])]});}
            var Q8;
            Q8=makeQuery(id+"F0.imprint","IMPRINT",FACE,{"disambiguationData":[TD([[makeQuery(id+"F0.imprint","IMPRINT",EDGE,{"derivedFrom":sQuery(id+"F0.wireOp",EDGE,"E99.trimOffspring")}),-1.0]])]});
            var Q9;
            Q9=makeQuery(id+"F0.imprint","IMPRINT",FACE,{"disambiguationData":[TD([[makeQuery(id+"F0.imprint","IMPRINT",EDGE,{"derivedFrom":sQuery(id+"F0.wireOp",EDGE,"E90.trimOffspring")}),-1.0]])]});
            var Q10;
            Q10=makeQuery(id+"F0.imprint","IMPRINT",FACE,{"disambiguationData":[TD([[makeQuery(id+"F0.imprint","IMPRINT",EDGE,{"derivedFrom":sQuery(id+"F0.wireOp",EDGE,"E44")}),-1.0]])]});
            var Q11;
            {var subQ0=sQuery(id+"F0.wireOp",EDGE,"E51");Q11=makeQuery(id+"F0.imprint","IMPRINT",FACE,{"disambiguationData":[TD([[makeQuery(id+"F0.imprint","IMPRINT",EDGE,{"derivedFrom":subQ0}),1.0]])]});}
            var Q12;
            Q12=makeQuery(id+"F0.imprint","IMPRINT",FACE,{"disambiguationData":[TD([[makeQuery(id+"F0.imprint","IMPRINT",EDGE,{"derivedFrom":sQuery(id+"F0.wireOp",EDGE,"E107.trimOffspring")}),1.0]])]});
            var Q13;
            {var subQ0=sQuery(id+"F0.wireOp",EDGE,"E17");Q13=makeQuery(id+"F0.imprint","IMPRINT",FACE,{"disambiguationData":[TD([[makeQuery(id+"F0.imprint","IMPRINT",EDGE,{"derivedFrom":subQ0}),1.0]])]});}
            var Q14;
            {var subQ0=sQuery(id+"F0.wireOp",EDGE,"E19");Q14=makeQuery(id+"F0.imprint","IMPRINT",FACE,{"disambiguationData":[TD([[makeQuery(id+"F0.imprint","IMPRINT",EDGE,{"derivedFrom":subQ0}),1.0]])]});}
            var Q15;
            Q15=makeQuery(id+"F0.imprint","IMPRINT",FACE,{"disambiguationData":[TD([[makeQuery(id+"F0.imprint","IMPRINT",EDGE,{"derivedFrom":sQuery(id+"F0.wireOp",EDGE,"E116.trimOffspring")}),1.0]])]});
            var Q16;
            Q16=makeQuery(id+"F0.imprint","IMPRINT",FACE,{"disambiguationData":[TD([[makeQuery(id+"F0.imprint","IMPRINT",EDGE,{"derivedFrom":sQuery(id+"F0.wireOp",EDGE,"E144.trimOffspring")}),1.0]])]});
            var Q17;
            {var subQ0=sQuery(id+"F0.wireOp",EDGE,"E21");Q17=makeQuery(id+"F0.imprint","IMPRINT",FACE,{"disambiguationData":[TD([[makeQuery(id+"F0.imprint","IMPRINT",EDGE,{"derivedFrom":subQ0}),1.0]])]});}
            var Q18;
            Q18=makeQuery(id+"F0.imprint","IMPRINT",FACE,{"disambiguationData":[TD([[makeQuery(id+"F0.imprint","IMPRINT",EDGE,{"derivedFrom":sQuery(id+"F0.wireOp",EDGE,"E148.trimOffspring")}),1.0]])]});
            var Q19;
            {var subQ0=sQuery(id+"F0.wireOp",EDGE,"E23");Q19=makeQuery(id+"F0.imprint","IMPRINT",FACE,{"disambiguationData":[TD([[makeQuery(id+"F0.imprint","IMPRINT",EDGE,{"derivedFrom":subQ0}),1.0]])]});}
            var Q20;
            {var subQ0=sQuery(id+"F0.wireOp",EDGE,"E25");Q20=makeQuery(id+"F0.imprint","IMPRINT",FACE,{"disambiguationData":[TD([[makeQuery(id+"F0.imprint","IMPRINT",EDGE,{"derivedFrom":subQ0}),1.0]])]});}
            var Q21;
            Q21=makeQuery(id+"F0.imprint","IMPRINT",FACE,{"disambiguationData":[TD([[makeQuery(id+"F0.imprint","IMPRINT",EDGE,{"derivedFrom":sQuery(id+"F0.wireOp",EDGE,"E214.trimOffspring")}),-1.0]])]});
            var Q22;
            {var subQ1=sQuery(id+"F0.wireOp",EDGE,"E268");Q22=makeQuery(id+"F0.imprint","IMPRINT",FACE,{"disambiguationData":[TD([[makeQuery(id+"F0.imprint","IMPRINT",EDGE,{"derivedFrom":subQ1}),-1.0]])]});}
            var Q23;
            Q23=makeQuery(id+"F0.imprint","IMPRINT",FACE,{"disambiguationData":[TD([[makeQuery(id+"F0.imprint","IMPRINT",EDGE,{"derivedFrom":sQuery(id+"F0.wireOp",EDGE,"E217.trimOffspring")}),-1.0]])]});
            var Q24;
            Q24=makeQuery(id+"F0.imprint","IMPRINT",FACE,{"disambiguationData":[TD([[makeQuery(id+"F0.imprint","IMPRINT",EDGE,{"derivedFrom":sQuery(id+"F0.wireOp",EDGE,"E217.trimOffspring")}),-1.0]])]});
            var Q25;
            {var subQ0=sQuery(id+"F0.wireOp",EDGE,"E27");Q25=makeQuery(id+"F0.imprint","IMPRINT",FACE,{"disambiguationData":[TD([[makeQuery(id+"F0.imprint","IMPRINT",EDGE,{"derivedFrom":subQ0}),1.0]])]});}
            var Q26;
            Q26=makeQuery(id+"F0.imprint","IMPRINT",FACE,{"disambiguationData":[TD([[makeQuery(id+"F0.imprint","IMPRINT",EDGE,{"derivedFrom":sQuery(id+"F0.wireOp",EDGE,"E219.trimOffspring")}),1.0]])]});
            var Q27;
            Q27=makeQuery(id+"F0.imprint","IMPRINT",FACE,{"disambiguationData":[TD([[makeQuery(id+"F0.imprint","IMPRINT",EDGE,{"derivedFrom":sQuery(id+"F0.wireOp",EDGE,"E46")}),1.0]])]});
            var Q28;
            Q28=makeQuery(id+"F0.imprint","IMPRINT",FACE,{"disambiguationData":[TD([[makeQuery(id+"F0.imprint","IMPRINT",EDGE,{"derivedFrom":sQuery(id+"F0.wireOp",EDGE,"E221.trimOffspring")}),-1.0]])]});
            var Q29;
            Q29=makeQuery(id+"F0.imprint","IMPRINT",FACE,{"disambiguationData":[TD([[makeQuery(id+"F0.imprint","IMPRINT",EDGE,{"derivedFrom":sQuery(id+"F0.wireOp",EDGE,"E30")}),1.0]])]});
            var Q30;
            {var subQ1=sQuery(id+"F0.wireOp",EDGE,"E28");Q30=makeQuery(id+"F0.imprint","IMPRINT",FACE,{"disambiguationData":[TD([[makeQuery(id+"F0.imprint","IMPRINT",EDGE,{"derivedFrom":subQ1}),-1.0]])]});}
            var Q31;
            {var subQ0=sQuery(id+"F0.wireOp",EDGE,"E29");Q31=makeQuery(id+"F0.imprint","IMPRINT",FACE,{"disambiguationData":[TD([[makeQuery(id+"F0.imprint","IMPRINT",EDGE,{"derivedFrom":subQ0}),1.0]])]});}
            var Q32;
            Q32=makeQuery(id+"F0.imprint","IMPRINT",FACE,{"disambiguationData":[TD([[makeQuery(id+"F0.imprint","IMPRINT",EDGE,{"derivedFrom":sQuery(id+"F0.wireOp",EDGE,"E31")}),-1.0]])]});
            var Q33;
            {var subQ0=sQuery(id+"F0.wireOp",EDGE,"E265");Q33=makeQuery(id+"F0.imprint","IMPRINT",FACE,{"disambiguationData":[TD([[makeQuery(id+"F0.imprint","IMPRINT",EDGE,{"derivedFrom":subQ0}),1.0]])]});}
            var Q34;
            Q34=makeQuery(id+"F0.imprint","IMPRINT",FACE,{"disambiguationData":[TD([[makeQuery(id+"F0.imprint","IMPRINT",EDGE,{"derivedFrom":sQuery(id+"F0.wireOp",EDGE,"E150.trimOffspring")}),-1.0]])]});
            var Q35;
            Q35=makeQuery(id+"F0.imprint","IMPRINT",FACE,{"disambiguationData":[TD([[makeQuery(id+"F0.imprint","IMPRINT",EDGE,{"derivedFrom":sQuery(id+"F0.wireOp",EDGE,"E151.trimOffspring")}),-1.0]])]});
            var Q36;
            {var subQ2=sQuery(id+"F0.wireOp",EDGE,"E50");Q36=makeQuery(id+"F0.imprint","IMPRINT",FACE,{"disambiguationData":[TD([[makeQuery(id+"F0.imprint","IMPRINT",EDGE,{"derivedFrom":subQ2}),1.0]])]});}
            var Q37;
            Q37=makeQuery(id+"F0.imprint","IMPRINT",FACE,{"disambiguationData":[TD([[makeQuery(id+"F0.imprint","IMPRINT",EDGE,{"derivedFrom":sQuery(id+"F0.wireOp",EDGE,"E103.trimOffspring")}),-1.0]])]});
            var Q38;
            Q38=makeQuery(id+"F0.imprint","IMPRINT",FACE,{"disambiguationData":[TD([[makeQuery(id+"F0.imprint","IMPRINT",EDGE,{"derivedFrom":sQuery(id+"F0.wireOp",EDGE,"E111.trimOffspring")}),-1.0]])]});
            var Q39;
            Q39=makeQuery(id+"F0.imprint","IMPRINT",FACE,{"disambiguationData":[TD([[makeQuery(id+"F0.imprint","IMPRINT",EDGE,{"derivedFrom":sQuery(id+"F0.wireOp",EDGE,"E119.trimOffspring")}),-1.0]])]});
            var Q40;
            {var subQ1=sQuery(id+"F0.wireOp",EDGE,"E15");Q40=makeQuery(id+"F0.imprint","IMPRINT",FACE,{"disambiguationData":[TD([[makeQuery(id+"F0.imprint","IMPRINT",EDGE,{"derivedFrom":subQ1}),-1.0]])]});}
            var Q41;
            Q41=makeQuery(id+"F0.imprint","IMPRINT",FACE,{"disambiguationData":[TD([[makeQuery(id+"F0.imprint","IMPRINT",EDGE,{"derivedFrom":sQuery(id+"F0.wireOp",EDGE,"E123.trimOffspring")}),-1.0]])]});
            var Q42;
            Q42=makeQuery(id+"F0.imprint","IMPRINT",FACE,{"disambiguationData":[TD([[makeQuery(id+"F0.imprint","IMPRINT",EDGE,{"derivedFrom":sQuery(id+"F0.wireOp",EDGE,"E134.trimOffspring")}),1.0]])]});
            var Q43;
            Q43=makeQuery(id+"F0.imprint","IMPRINT",FACE,{"disambiguationData":[TD([[makeQuery(id+"F0.imprint","IMPRINT",EDGE,{"derivedFrom":sQuery(id+"F0.wireOp",EDGE,"E157.trimOffspring")}),1.0]])]});
            var Q44;
            {var subQ0=sQuery(id+"F0.wireOp",EDGE,"E255");Q44=makeQuery(id+"F0.imprint","IMPRINT",FACE,{"disambiguationData":[TD([[makeQuery(id+"F0.imprint","IMPRINT",EDGE,{"derivedFrom":subQ0}),-1.0]])]});}
            var Q45;
            {var subQ0=sQuery(id+"F0.wireOp",EDGE,"E49");Q45=makeQuery(id+"F0.imprint","IMPRINT",FACE,{"disambiguationData":[TD([[makeQuery(id+"F0.imprint","IMPRINT",EDGE,{"derivedFrom":subQ0}),-1.0]])]});}
            var Q46;
            {var subQ0=sQuery(id+"F0.wireOp",EDGE,"E52");Q46=makeQuery(id+"F0.imprint","IMPRINT",FACE,{"disambiguationData":[TD([[makeQuery(id+"F0.imprint","IMPRINT",EDGE,{"derivedFrom":subQ0}),-1.0]])]});}
            var Q47;
            {var subQ0=sQuery(id+"F0.wireOp",EDGE,"E53");Q47=makeQuery(id+"F0.imprint","IMPRINT",FACE,{"disambiguationData":[TD([[makeQuery(id+"F0.imprint","IMPRINT",EDGE,{"derivedFrom":subQ0}),-1.0]])]});}
            var Q48;
            {var subQ1=sQuery(id+"F0.wireOp",EDGE,"E55");Q48=makeQuery(id+"F0.imprint","IMPRINT",FACE,{"disambiguationData":[TD([[makeQuery(id+"F0.imprint","IMPRINT",EDGE,{"derivedFrom":subQ1}),1.0]])]});}
            var Q49;
            Q49=makeQuery(id+"F0.imprint","IMPRINT",FACE,{"disambiguationData":[TD([[makeQuery(id+"F0.imprint","IMPRINT",EDGE,{"derivedFrom":sQuery(id+"F0.wireOp",EDGE,"E135.trimOffspring")}),-1.0]])]});
            var Q50;
            Q50=makeQuery(id+"F0.imprint","IMPRINT",FACE,{"disambiguationData":[TD([[makeQuery(id+"F0.imprint","IMPRINT",EDGE,{"derivedFrom":sQuery(id+"F0.wireOp",EDGE,"E163.trimOffspring")}),1.0]])]});
            var Q51;
            {var subQ3=sQuery(id+"F0.wireOp",EDGE,"E162.trimOffspring");Q51=makeQuery(id+"F0.imprint","IMPRINT",FACE,{"disambiguationData":[TD([[makeQuery(id+"F0.imprint","IMPRINT",EDGE,{"derivedFrom":subQ3}),1.0]])]});}
            var Q52;
            {var subQ2=sQuery(id+"F0.wireOp",EDGE,"E58");Q52=makeQuery(id+"F0.imprint","IMPRINT",FACE,{"disambiguationData":[TD([[makeQuery(id+"F0.imprint","IMPRINT",EDGE,{"derivedFrom":subQ2}),1.0]])]});}
            var Q53;
            {var subQ0=sQuery(id+"F0.wireOp",EDGE,"E56");Q53=makeQuery(id+"F0.imprint","IMPRINT",FACE,{"disambiguationData":[TD([[makeQuery(id+"F0.imprint","IMPRINT",EDGE,{"derivedFrom":subQ0}),-1.0]])]});}
            var Q54;
            {var subQ0=sQuery(id+"F0.wireOp",EDGE,"E251");Q54=makeQuery(id+"F0.imprint","IMPRINT",FACE,{"disambiguationData":[TD([[makeQuery(id+"F0.imprint","IMPRINT",EDGE,{"derivedFrom":subQ0}),-1.0]])]});}
            var Q55;
            {var subQ2=sQuery(id+"F0.wireOp",EDGE,"E39.trimOffspring");Q55=makeQuery(id+"F0.imprint","IMPRINT",FACE,{"disambiguationData":[TD([[makeQuery(id+"F0.imprint","IMPRINT",EDGE,{"derivedFrom":subQ2}),-1.0]])]});}
            var Q56;
            {var subQ3=sQuery(id+"F0.wireOp",EDGE,"E162.trimOffspring");Q56=makeQuery(id+"F0.imprint","IMPRINT",FACE,{"disambiguationData":[TD([[makeQuery(id+"F0.imprint","IMPRINT",EDGE,{"derivedFrom":subQ3}),1.0]])]});}
            var Q57;
            {var subQ2=sQuery(id+"F0.wireOp",EDGE,"E58");Q57=makeQuery(id+"F0.imprint","IMPRINT",FACE,{"disambiguationData":[TD([[makeQuery(id+"F0.imprint","IMPRINT",EDGE,{"derivedFrom":subQ2}),1.0]])]});}
            var Q58;
            {var subQ0=sQuery(id+"F0.wireOp",EDGE,"E57");Q58=makeQuery(id+"F0.imprint","IMPRINT",FACE,{"disambiguationData":[TD([[makeQuery(id+"F0.imprint","IMPRINT",EDGE,{"derivedFrom":subQ0}),-1.0]])]});}
            var Q59;
            {var subQ1=sQuery(id+"F0.wireOp",EDGE,"E59");Q59=makeQuery(id+"F0.imprint","IMPRINT",FACE,{"disambiguationData":[TD([[makeQuery(id+"F0.imprint","IMPRINT",EDGE,{"derivedFrom":subQ1}),1.0]])]});}
            var Q60;
            Q60=makeQuery(id+"F0.imprint","IMPRINT",FACE,{"disambiguationData":[TD([[makeQuery(id+"F0.imprint","IMPRINT",EDGE,{"derivedFrom":sQuery(id+"F0.wireOp",EDGE,"E168.trimOffspring")}),1.0]])]});
            var Q61;
            {var subQ1=sQuery(id+"F0.wireOp",EDGE,"E37.trimOffspring");Q61=makeQuery(id+"F0.imprint","IMPRINT",FACE,{"disambiguationData":[TD([[makeQuery(id+"F0.imprint","IMPRINT",EDGE,{"derivedFrom":subQ1}),-1.0]])]});}
            var Q62;
            {var subQ1=sQuery(id+"F0.wireOp",EDGE,"E62");Q62=makeQuery(id+"F0.imprint","IMPRINT",FACE,{"disambiguationData":[TD([[makeQuery(id+"F0.imprint","IMPRINT",EDGE,{"derivedFrom":subQ1}),1.0]])]});}
            var Q63;
            Q63=makeQuery(id+"F0.imprint","IMPRINT",FACE,{"disambiguationData":[TD([[makeQuery(id+"F0.imprint","IMPRINT",EDGE,{"derivedFrom":sQuery(id+"F0.wireOp",EDGE,"E180.trimOffspring")}),1.0]])]});
            var Q64;
            Q64=makeQuery(id+"F0.imprint","IMPRINT",FACE,{"disambiguationData":[TD([[makeQuery(id+"F0.imprint","IMPRINT",EDGE,{"derivedFrom":sQuery(id+"F0.wireOp",EDGE,"E36.trimOffspring")}),1.0]])]});
            var Q65;
            Q65=makeQuery(id+"F0.imprint","IMPRINT",FACE,{"disambiguationData":[TD([[makeQuery(id+"F0.imprint","IMPRINT",EDGE,{"derivedFrom":sQuery(id+"F0.wireOp",EDGE,"E35.trimOffspring")}),-1.0]])]});
            var Q66;
            {var subQ0=sQuery(id+"F0.wireOp",EDGE,"E63");Q66=makeQuery(id+"F0.imprint","IMPRINT",FACE,{"disambiguationData":[TD([[makeQuery(id+"F0.imprint","IMPRINT",EDGE,{"derivedFrom":subQ0}),1.0]])]});}
            var Q67;
            {var subQ0=sQuery(id+"F0.wireOp",EDGE,"E66");Q67=makeQuery(id+"F0.imprint","IMPRINT",FACE,{"disambiguationData":[TD([[makeQuery(id+"F0.imprint","IMPRINT",EDGE,{"derivedFrom":subQ0}),1.0]])]});}
            var Q68;
            {var subQ0=sQuery(id+"F0.wireOp",EDGE,"E34.trimOffspring");Q68=makeQuery(id+"F0.imprint","IMPRINT",FACE,{"disambiguationData":[TD([[makeQuery(id+"F0.imprint","IMPRINT",EDGE,{"derivedFrom":subQ0}),1.0]])]});}
            var Q69;
            Q69=makeQuery(id+"F0.imprint","IMPRINT",FACE,{"disambiguationData":[TD([[makeQuery(id+"F0.imprint","IMPRINT",EDGE,{"derivedFrom":sQuery(id+"F0.wireOp",EDGE,"E32")}),-1.0]])]});
            var Q70;
            {var subQ1=sQuery(id+"F0.wireOp",EDGE,"E67");Q70=makeQuery(id+"F0.imprint","IMPRINT",FACE,{"disambiguationData":[TD([[makeQuery(id+"F0.imprint","IMPRINT",EDGE,{"derivedFrom":subQ1}),1.0]])]});}
            var Q71;
            {var subQ0=sQuery(id+"F0.wireOp",EDGE,"E33");Q71=makeQuery(id+"F0.imprint","IMPRINT",FACE,{"disambiguationData":[TD([[makeQuery(id+"F0.imprint","IMPRINT",EDGE,{"derivedFrom":subQ0}),1.0]])]});}
            var Q72;
            {var subQ4=sQuery(id+"F0.wireOp",EDGE,"E202.trimOffspring");Q72=makeQuery(id+"F0.imprint","IMPRINT",FACE,{"disambiguationData":[TD([[makeQuery(id+"F0.imprint","IMPRINT",EDGE,{"derivedFrom":subQ4}),-1.0]])]});}
            var Q73;
            Q73=makeQuery(id+"F0.imprint","IMPRINT",FACE,{"disambiguationData":[TD([[makeQuery(id+"F0.imprint","IMPRINT",EDGE,{"derivedFrom":sQuery(id+"F0.wireOp",EDGE,"E210.trimOffspring")}),-1.0]])]});
            var Q74;
            {var subQ0=sQuery(id+"F0.wireOp",EDGE,"E38.trimOffspring");Q74=makeQuery(id+"F0.imprint","IMPRINT",FACE,{"disambiguationData":[TD([[makeQuery(id+"F0.imprint","IMPRINT",EDGE,{"derivedFrom":subQ0}),1.0]])]});}
            var Q75;
            {var subQ0=sQuery(id+"F0.wireOp",EDGE,"E60");Q75=makeQuery(id+"F0.imprint","IMPRINT",FACE,{"disambiguationData":[TD([[makeQuery(id+"F0.imprint","IMPRINT",EDGE,{"derivedFrom":subQ0}),-1.0]])]});}
            var Q76;
            {var subQ0=sQuery(id+"F0.wireOp",EDGE,"E61");Q76=makeQuery(id+"F0.imprint","IMPRINT",FACE,{"disambiguationData":[TD([[makeQuery(id+"F0.imprint","IMPRINT",EDGE,{"derivedFrom":subQ0}),-1.0]])]});}
            var Q77;
            {var subQ0=sQuery(id+"F0.wireOp",EDGE,"E64");Q77=makeQuery(id+"F0.imprint","IMPRINT",FACE,{"disambiguationData":[TD([[makeQuery(id+"F0.imprint","IMPRINT",EDGE,{"derivedFrom":subQ0}),-1.0]])]});}
            var Q78;
            {var subQ0=sQuery(id+"F0.wireOp",EDGE,"E65");Q78=makeQuery(id+"F0.imprint","IMPRINT",FACE,{"disambiguationData":[TD([[makeQuery(id+"F0.imprint","IMPRINT",EDGE,{"derivedFrom":subQ0}),-1.0]])]});}
            var Q79;
            {var subQ0=sQuery(id+"F0.wireOp",EDGE,"E68");Q79=makeQuery(id+"F0.imprint","IMPRINT",FACE,{"disambiguationData":[TD([[makeQuery(id+"F0.imprint","IMPRINT",EDGE,{"derivedFrom":subQ0}),-1.0]])]});}
            extrude(context, id + "F3", {"entities" : qUnion([Q0, Q1, Q2, Q3, Q4, Q5, Q6, Q7, Q8, Q9, Q10, Q11, Q12, Q13, Q14, Q15, Q16, Q17, Q18, Q19, Q20, Q21, Q22, Q23, Q24, Q25, Q26, Q27, Q28, Q29, Q30, Q31, Q32, Q33, Q34, Q35, Q36, Q37, Q38, Q39, Q40, Q41, Q42, Q43, Q44, Q45, Q46, Q47, Q48, Q49, Q50, Q51, Q52, Q53, Q54, Q55, Q56, Q57, Q58, Q59, Q60, Q61, Q62, Q63, Q64, Q65, Q66, Q67, Q68, Q69, Q70, Q71, Q72, Q73, Q74, Q75, Q76, Q77, Q78, Q79]), "operationType" : NewBodyOperationType.ADD, "oppositeDirection" : true, "depth" : 3.12 * mm});
        }
        {
            var Q0;
            Q0=makeQuery(id+"F1.opExtrude","CAP_EDGE",EDGE,{"disambiguationData":[OSD([sQuery(id+"F0.wireOp",EDGE,"E4")])],"isStart":false});
            var Q1;
            Q1=makeQuery(id+"F1.opExtrude","CAP_EDGE",EDGE,{"disambiguationData":[OSD([sQuery(id+"F0.wireOp",EDGE,"E4")])],"isStart":true});
            var Q2;
            Q2=makeQuery(id+"F1.opExtrude","CAP_EDGE",EDGE,{"disambiguationData":[OSD([sQuery(id+"F0.wireOp",EDGE,"E5")])],"isStart":false});
            var Q3;
            Q3=makeQuery(id+"F1.opExtrude","CAP_EDGE",EDGE,{"disambiguationData":[OSD([sQuery(id+"F0.wireOp",EDGE,"E5")])],"isStart":true});
            var Q4;
            Q4=makeQuery(id+"F1.opExtrude","CAP_EDGE",EDGE,{"disambiguationData":[OSD([sQuery(id+"F0.wireOp",EDGE,"E244")])],"isStart":false});
            var Q5;
            Q5=makeQuery(id+"F1.opExtrude","CAP_EDGE",EDGE,{"disambiguationData":[OSD([sQuery(id+"F0.wireOp",EDGE,"E244")])],"isStart":true});
            var Q6;
            Q6=makeQuery(id+"F1.opExtrude","CAP_EDGE",EDGE,{"disambiguationData":[OSD([sQuery(id+"F0.wireOp",EDGE,"E6")])],"isStart":false});
            var Q7;
            Q7=makeQuery(id+"F1.opExtrude","CAP_EDGE",EDGE,{"disambiguationData":[OSD([sQuery(id+"F0.wireOp",EDGE,"E6")])],"isStart":true});
            var Q8;
            Q8=makeQuery(id+"F1.opExtrude","CAP_EDGE",EDGE,{"disambiguationData":[OSD([sQuery(id+"F0.wireOp",EDGE,"E0")])],"isStart":false});
            var Q9;
            Q9=makeQuery(id+"F1.opExtrude","CAP_EDGE",EDGE,{"disambiguationData":[OSD([sQuery(id+"F0.wireOp",EDGE,"E0")])],"isStart":true});
            var Q10;
            Q10=makeQuery(id+"F1.opExtrude","SWEPT_EDGE",EDGE,{"disambiguationData":[OSD([sQuery(id+"F0.wireOp",EDGE,"E0"),sQuery(id+"F0.wireOp",EDGE,"E1")])]});
            var Q11;
            Q11=makeQuery(id+"F1.opExtrude","SWEPT_EDGE",EDGE,{"disambiguationData":[OSD([sQuery(id+"F0.wireOp",EDGE,"E4"),sQuery(id+"F0.wireOp",EDGE,"E278")])]});
            fillet(context, id + "F4", {"entities" : qUnion([Q0, Q1, Q2, Q3, Q4, Q5, Q6, Q7, Q8, Q9, Q10, Q11]), "radius" : 2 * mm, "tangentPropagation" : true, "allowEdgeOverflow" : false});
        }
    });
